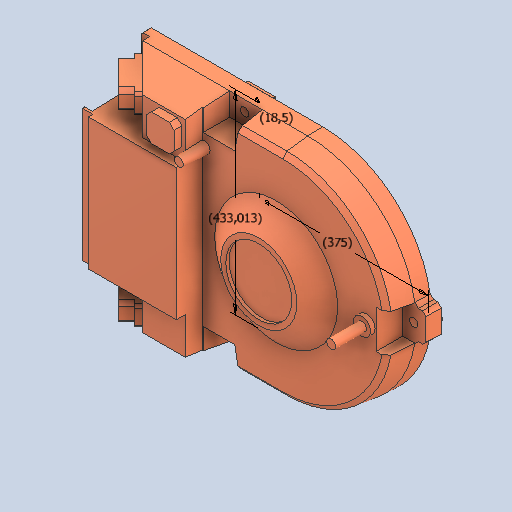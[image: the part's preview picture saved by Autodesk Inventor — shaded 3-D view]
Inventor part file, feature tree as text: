
AUTODESK INVENTOR PART (.ipt)
format: ipt  version: 2024 (Build 280153000, 153)  size: 279,040 bytes
history: native  units: in
note: dims shown in document units (in); Inventor stores cm internally (conversion verified against a paired STEP export)
features: other x2, sketch x1
ambient origin geometry x8: Origin, YZ Plane, XZ Plane, XY Plane, X Axis, Y Axis, Z Axis, Center Point
bodies: Body1 (feature_tree)
feature tree (3):
  other  "Sólido1"
  sketch  "Boceto1"  dims[d0=14.7638in d1=17.0477in d2=0.7283in]
  parser-record x1  (decoder bookkeeping rows leaked as tree rows — omitted from the tree; the rows remain in map.json)
